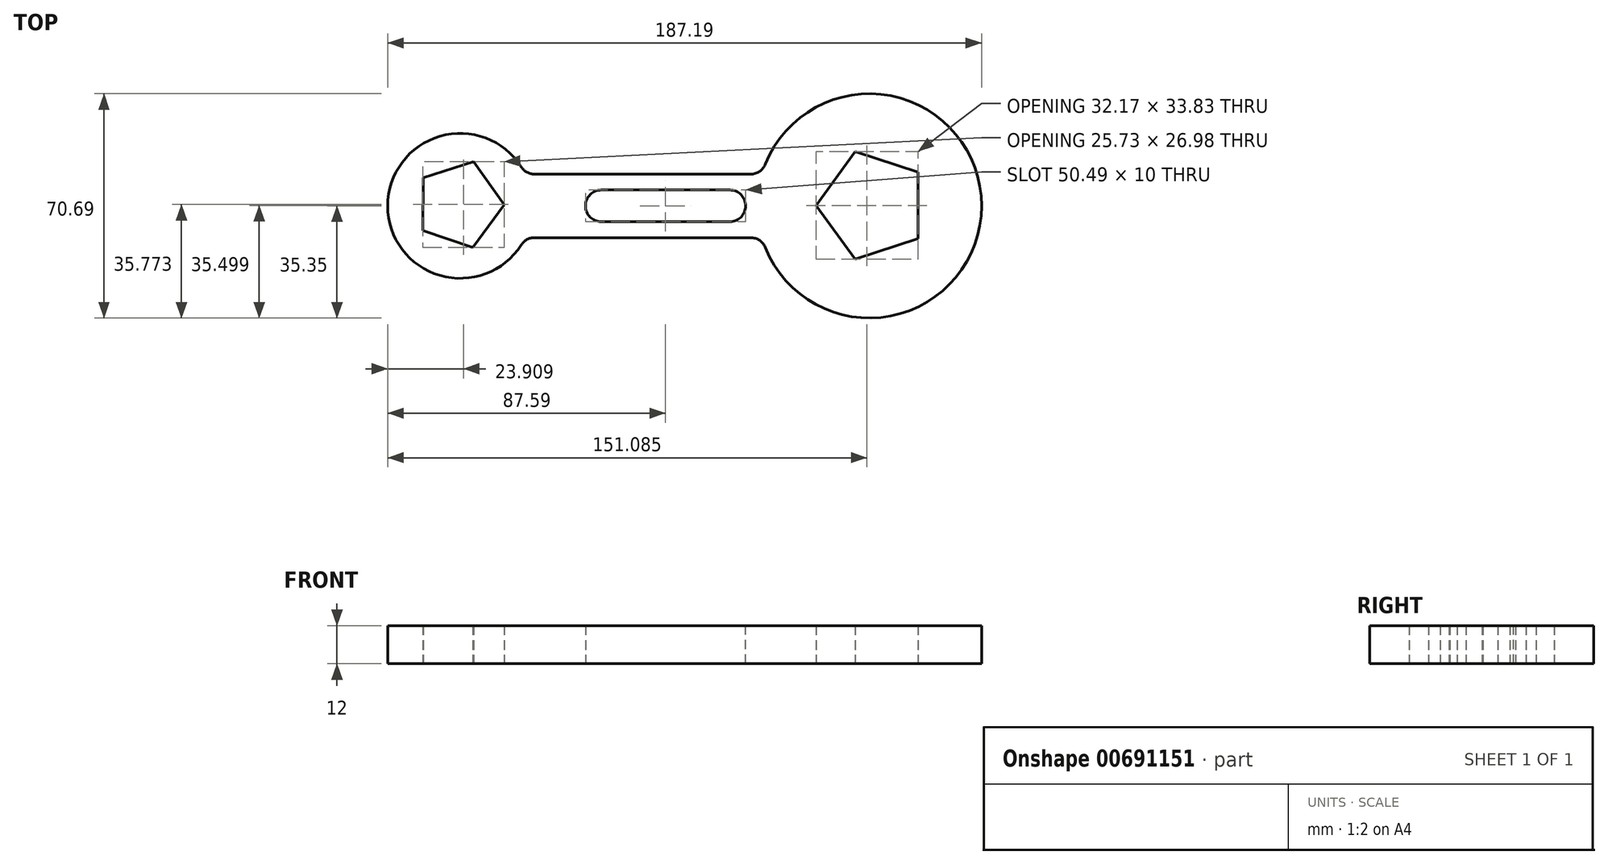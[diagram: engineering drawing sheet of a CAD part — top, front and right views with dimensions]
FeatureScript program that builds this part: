
annotation { "Feature Type Name" : "Feature", "Feature Type Description" : "" }
export const myFeature = defineFeature(function(context is Context, id is Id, definition is map)
    precondition{}
    {
        {
            var Q0;
            Q0=qCreatedBy(makeId("Top.planeOp"),FACE);
            var sketch = newSketch(context, id + "F0", { "sketchPlane" : qUnion([Q0])});
            skLineSegment(sketch, "E0.bottom", {"start": v(64.26, 0) * mm, "end": v(-64.74, 0) * mm});
            skLineSegment(sketch, "E0.top", {"start": v(64.26, 20) * mm, "end": v(-64.74, 20) * mm});
            skLineSegment(sketch, "E0.left", {"start": v(64.26, 0) * mm, "end": v(64.26, 20) * mm});
            skLineSegment(sketch, "E0.right", {"start": v(-64.74, 0) * mm, "end": v(-64.74, 20) * mm});
            skPoint(sketch, "E0.middle", {"position": v(-0.24, 10) * mm});
            skSolve(sketch);
        }
        {
            var Q0;
            Q0=makeQuery(id+"F0.imprint","IMPRINT",FACE,{"disambiguationData":[TD([[makeQuery(id+"F0.imprint","IMPRINT",EDGE,{"derivedFrom":sQuery(id+"F0.wireOp",EDGE,"E0.bottom")}),-1.0]])]});
            extrude(context, id + "F1", {"entities" : qUnion([Q0]), "depth" : 12 * mm, "offsetDistance" : 25 * mm});
        }
        {
            var Q0;
            Q0=qCreatedBy(makeId("Top.planeOp"),FACE);
            var sketch = newSketch(context, id + "F2", { "sketchPlane" : qUnion([Q0])});
            skCircle(sketch, "E1", {"center": v(-64.74, 10) * mm, "radius": 22.85 * mm});
            skSolve(sketch);
        }
        {
            var Q0;
            Q0=qCreatedBy(makeId("Top.planeOp"),FACE);
            var sketch = newSketch(context, id + "F3", { "sketchPlane" : qUnion([Q0])});
            skCircle(sketch, "E2", {"center": v(64.26, 10) * mm, "radius": 35.35 * mm});
            skSolve(sketch);
        }
        {
            var Q0;
            Q0=makeQuery(id+"F2.imprint","IMPRINT",FACE,{"disambiguationData":[TD([[makeQuery(id+"F2.imprint","IMPRINT",EDGE,{"derivedFrom":sQuery(id+"F2.wireOp",EDGE,"E1")}),1.0]])]});
            extrude(context, id + "F4", {"entities" : qUnion([Q0]), "operationType" : NewBodyOperationType.ADD, "depth" : 12 * mm, "offsetDistance" : 25 * mm});
        }
        {
            var Q0;
            Q0=makeQuery(id+"F3.imprint","IMPRINT",FACE,{"disambiguationData":[TD([[makeQuery(id+"F3.imprint","IMPRINT",EDGE,{"derivedFrom":sQuery(id+"F3.wireOp",EDGE,"E2")}),1.0]])]});
            extrude(context, id + "F5", {"entities" : qUnion([Q0]), "operationType" : NewBodyOperationType.ADD, "depth" : 12 * mm, "offsetDistance" : 25 * mm});
        }
        {
            var Q0;
            Q0=qCreatedBy(makeId("Top.planeOp"),FACE);
            var sketch = newSketch(context, id + "F6", { "sketchPlane" : qUnion([Q0])});
            skLineSegment(sketch, "E3.bottom", {"start": v(25.24, 5) * mm, "end": v(-25.24, 5) * mm});
            skLineSegment(sketch, "E3.top", {"start": v(25.24, 15) * mm, "end": v(-25.24, 15) * mm});
            skLineSegment(sketch, "E3.left", {"start": v(25.24, 5) * mm, "end": v(25.24, 15) * mm});
            skLineSegment(sketch, "E3.right", {"start": v(-25.24, 5) * mm, "end": v(-25.24, 15) * mm});
            skPoint(sketch, "E3.middle", {"position": v(0, 10) * mm});
            skSolve(sketch);
        }
        {
            var Q0;
            Q0 = qSketchRegion(id + "F6", true);
            extrude(context, id + "F7", {"entities" : qUnion([Q0]), "operationType" : NewBodyOperationType.ADD, "depth" : 12 * mm, "offsetDistance" : 25 * mm});
        }
        {
            var Q0;
            Q0 = qSketchRegion(id + "F6", true);
            extrude(context, id + "F8", {"entities" : qUnion([Q0]), "operationType" : NewBodyOperationType.REMOVE, "depth" : 12 * mm, "offsetDistance" : 25 * mm});
        }
        {
            var Q0;
            Q0=makeQuery(id+"F8.boolean.opBoolean","COPY",EDGE,{"derivedFrom":makeQuery(id+"F8.opExtrude","SWEPT_EDGE",EDGE,{"disambiguationData":[OSD([sQuery(id+"F6.wireOp",EDGE,"E3.top"),sQuery(id+"F6.wireOp",EDGE,"E3.right")])]})});
            var Q1;
            Q1=makeQuery(id+"F8.boolean.opBoolean","COPY",EDGE,{"derivedFrom":makeQuery(id+"F8.opExtrude","SWEPT_EDGE",EDGE,{"disambiguationData":[OSD([sQuery(id+"F6.wireOp",EDGE,"E3.top"),sQuery(id+"F6.wireOp",EDGE,"E3.left")])]})});
            var Q2;
            Q2=makeQuery(id+"F8.boolean.opBoolean","COPY",EDGE,{"derivedFrom":makeQuery(id+"F8.opExtrude","SWEPT_EDGE",EDGE,{"disambiguationData":[OSD([sQuery(id+"F6.wireOp",EDGE,"E3.bottom"),sQuery(id+"F6.wireOp",EDGE,"E3.left")])]})});
            var Q3;
            Q3=makeQuery(id+"F8.boolean.opBoolean","COPY",EDGE,{"derivedFrom":makeQuery(id+"F8.opExtrude","SWEPT_EDGE",EDGE,{"disambiguationData":[OSD([sQuery(id+"F6.wireOp",EDGE,"E3.bottom"),sQuery(id+"F6.wireOp",EDGE,"E3.right")])]})});
            fillet(context, id + "F9", {"entities" : qUnion([Q0, Q1, Q2, Q3]), "radius" : 5 * mm, "tangentPropagation" : true, "allowEdgeOverflow" : false});
        }
        {
            var Q0;
            Q0=makeQuery(id+"F2.imprint","IMPRINT",FACE,{"disambiguationData":[TD([[makeQuery(id+"F2.imprint","IMPRINT",EDGE,{"derivedFrom":sQuery(id+"F2.wireOp",EDGE,"E1")}),1.0]])]});
            var sketch = newSketch(context, id + "F10", { "sketchPlane" : qUnion([Q0])});
            skCircle(sketch, "E4.cCircle", {"center": v(-65, 10.46) * mm, "radius": 11.48 * mm, "construction": true});
            skLineSegment(sketch, "E4.0", {"start": v(-50.82, 10.34) * mm, "end": v(-60.73, -3.07) * mm});
            skLineSegment(sketch, "E4.1", {"start": v(-60.73, -3.07) * mm, "end": v(-76.55, 2.22) * mm});
            skLineSegment(sketch, "E4.2", {"start": v(-76.55, 2.22) * mm, "end": v(-76.4, 18.9) * mm});
            skLineSegment(sketch, "E4.3", {"start": v(-76.4, 18.9) * mm, "end": v(-60.5, 23.91) * mm});
            skLineSegment(sketch, "E4.4", {"start": v(-60.5, 23.91) * mm, "end": v(-50.82, 10.34) * mm});
            skPoint(sketch, "E4.0.midPoint", {"position": v(-55.78, 3.64) * mm});
            skSolve(sketch);
        }
        {
            var Q0;
            Q0 = qSketchRegion(id + "F10", true);
            extrude(context, id + "F11", {"entities" : qUnion([Q0]), "operationType" : NewBodyOperationType.REMOVE, "depth" : 12 * mm, "offsetDistance" : 25 * mm});
        }
        {
            var Q0;
            Q0=makeQuery(id+"F3.imprint","IMPRINT",FACE,{"disambiguationData":[TD([[makeQuery(id+"F3.imprint","IMPRINT",EDGE,{"derivedFrom":sQuery(id+"F3.wireOp",EDGE,"E2")}),1.0]])]});
            var sketch = newSketch(context, id + "F12", { "sketchPlane" : qUnion([Q0])});
            skCircle(sketch, "E5.cCircle", {"center": v(65.2, 10.15) * mm, "radius": 14.39 * mm, "construction": true});
            skLineSegment(sketch, "E5.0", {"start": v(79.58, 20.6) * mm, "end": v(79.58, -0.3) * mm});
            skLineSegment(sketch, "E5.1", {"start": v(79.58, -0.3) * mm, "end": v(59.7, -6.77) * mm});
            skLineSegment(sketch, "E5.2", {"start": v(59.7, -6.77) * mm, "end": v(47.4, 10.15) * mm});
            skLineSegment(sketch, "E5.3", {"start": v(47.4, 10.15) * mm, "end": v(59.7, 27.06) * mm});
            skLineSegment(sketch, "E5.4", {"start": v(59.7, 27.06) * mm, "end": v(79.58, 20.6) * mm});
            skPoint(sketch, "E5.0.midPoint", {"position": v(79.58, 10.15) * mm});
            skSolve(sketch);
        }
        {
            var Q0;
            Q0 = qSketchRegion(id + "F12", true);
            extrude(context, id + "F13", {"entities" : qUnion([Q0]), "operationType" : NewBodyOperationType.REMOVE, "depth" : 12 * mm, "offsetDistance" : 25 * mm});
        }
        {
            var Q0;
            Q0=makeQuery(id+"F4.boolean.opBoolean","INTERSECT",EDGE,{"derivedFrom":[makeQuery(id+"F1.opExtrude","SWEPT_FACE",FACE,{"disambiguationData":[OSD([sQuery(id+"F0.wireOp",EDGE,"E0.bottom")])]}),makeQuery(id+"F4.opExtrude","SWEPT_FACE",FACE,{"disambiguationData":[OSD([sQuery(id+"F2.wireOp",EDGE,"E1")])]})]});
            var Q1;
            Q1=makeQuery(id+"F5.boolean.opBoolean","INTERSECT",EDGE,{"derivedFrom":[makeQuery(id+"F1.opExtrude","SWEPT_FACE",FACE,{"disambiguationData":[OSD([sQuery(id+"F0.wireOp",EDGE,"E0.bottom")])]}),makeQuery(id+"F5.opExtrude","SWEPT_FACE",FACE,{"disambiguationData":[OSD([sQuery(id+"F3.wireOp",EDGE,"E2")])]})]});
            var Q2;
            Q2=makeQuery(id+"F5.boolean.opBoolean","INTERSECT",EDGE,{"derivedFrom":[makeQuery(id+"F1.opExtrude","SWEPT_FACE",FACE,{"disambiguationData":[OSD([sQuery(id+"F0.wireOp",EDGE,"E0.top")])]}),makeQuery(id+"F5.opExtrude","SWEPT_FACE",FACE,{"disambiguationData":[OSD([sQuery(id+"F3.wireOp",EDGE,"E2")])]})]});
            var Q3;
            Q3=makeQuery(id+"F4.boolean.opBoolean","INTERSECT",EDGE,{"derivedFrom":[makeQuery(id+"F1.opExtrude","SWEPT_FACE",FACE,{"disambiguationData":[OSD([sQuery(id+"F0.wireOp",EDGE,"E0.top")])]}),makeQuery(id+"F4.opExtrude","SWEPT_FACE",FACE,{"disambiguationData":[OSD([sQuery(id+"F2.wireOp",EDGE,"E1")])]})]});
            fillet(context, id + "F14", {"entities" : qUnion([Q0, Q1, Q2, Q3]), "radius" : 5 * mm, "tangentPropagation" : true, "allowEdgeOverflow" : false});
        }
    });
